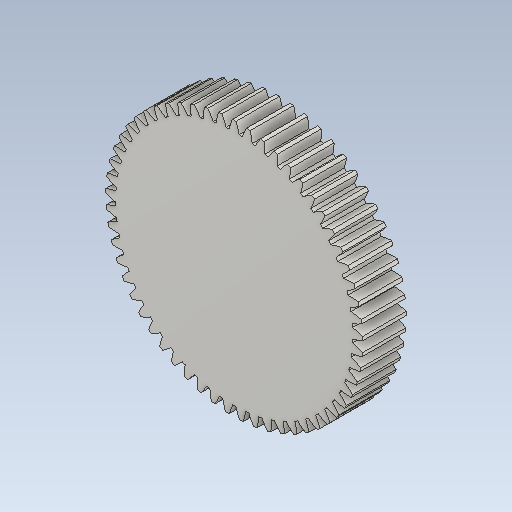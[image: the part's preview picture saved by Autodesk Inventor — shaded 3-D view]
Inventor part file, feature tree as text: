
AUTODESK INVENTOR PART (.ipt)
format: ipt  version: 2021 (Build 250183000, 183)  size: 400,384 bytes
history: native  units: mm (DEFAULTED — no unit token found)
features: plane x3, other x3, sketch x2, extrude x1
ambient origin geometry x8: Origin, YZ Plane, XZ Plane, XY Plane, X Axis, Y Axis, Z Axis, Center Point
bodies: Solid1 (feature_tree)
feature tree (9):
  extrude  "Extrusion1"  Depth=20.0mm TaperAngle=0.0deg
  plane  "Work Plane2"
  plane  "Work Plane8"
  plane  "Work Plane9"
  other  "Engrenage cylindrique"
  sketch  "Sketch1"  dims[d0=118.0mm d1=20.0mm d2=0.0mm]
  sketch  "Sketch2"  dims[d3=114.0mm d4=10.0mm d5=0.0mm d16=80.0mm d17=0.0mm d34=0.551157mm d39=0.0mm d41=0.0mm d43=80.0mm d46=80.0mm d47=0.0mm d48=0.0mm]
  other  "Srf1"
  other  "Diamètre primitif"
